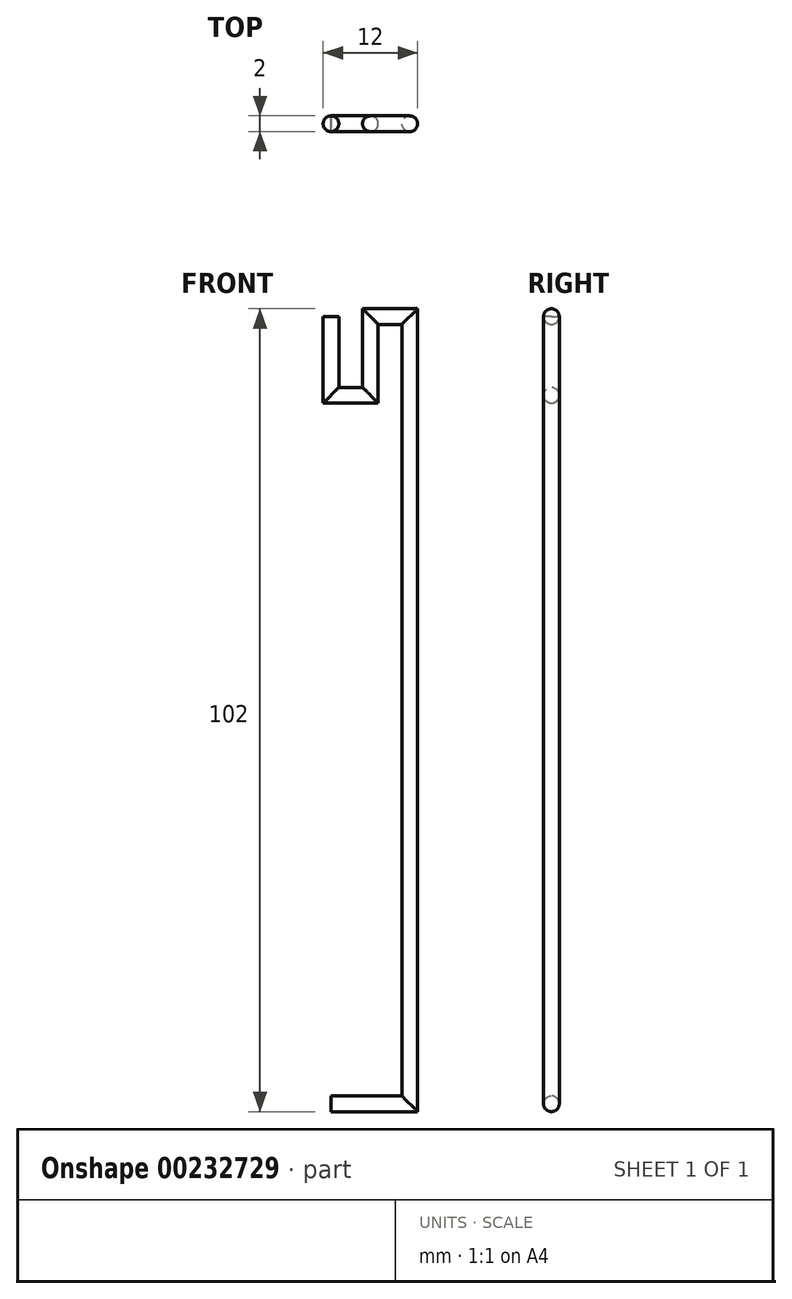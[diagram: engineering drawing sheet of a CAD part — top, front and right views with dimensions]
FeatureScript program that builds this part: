
annotation { "Feature Type Name" : "Feature", "Feature Type Description" : "" }
export const myFeature = defineFeature(function(context is Context, id is Id, definition is map)
    precondition{}
    {
        {
            var Q0;
            Q0=qCreatedBy(makeId("Top.planeOp"),FACE);
            var sketch = newSketch(context, id + "F0", { "sketchPlane" : qUnion([Q0])});
            skCircle(sketch, "E0", {"center": v(-25.42, 0) * mm, "radius": 1 * mm});
            skSolve(sketch);
        }
        {
            var Q0;
            Q0=qCreatedBy(makeId("Front.planeOp"),FACE);
            var sketch = newSketch(context, id + "F1", { "sketchPlane" : qUnion([Q0])});
            skPoint(sketch, "E1.0", {"position": v(-25.42, 0) * mm});
            skLineSegment(sketch, "E2", {"start": v(-25.42, 0) * mm, "end": v(-25.42, -10) * mm});
            skLineSegment(sketch, "E3", {"start": v(-20.42, -10) * mm, "end": v(-25.42, -10) * mm});
            skLineSegment(sketch, "E4", {"start": v(-20.42, -10) * mm, "end": v(-20.42, 0) * mm});
            skLineSegment(sketch, "E5", {"start": v(-20.42, 0) * mm, "end": v(-15.42, 0) * mm});
            skLineSegment(sketch, "E6", {"start": v(-15.42, 0) * mm, "end": v(-15.42, -100) * mm});
            skLineSegment(sketch, "E7", {"start": v(-15.42, -100) * mm, "end": v(-25.42, -100) * mm});
            skSolve(sketch);
        }
        {
            var Q0;
            Q0 = qSketchRegion(id + "F0", true);
            var Q1;
            Q1 = qConstructionFilter(qBodyType(qCreatedBy(id + "F1" ,EDGE), BodyType.WIRE), ConstructionObject.NO);
            sweep(context, id + "F2", {"profiles" : qUnion([Q0]), "path" : qUnion([Q1])});
        }
    });
